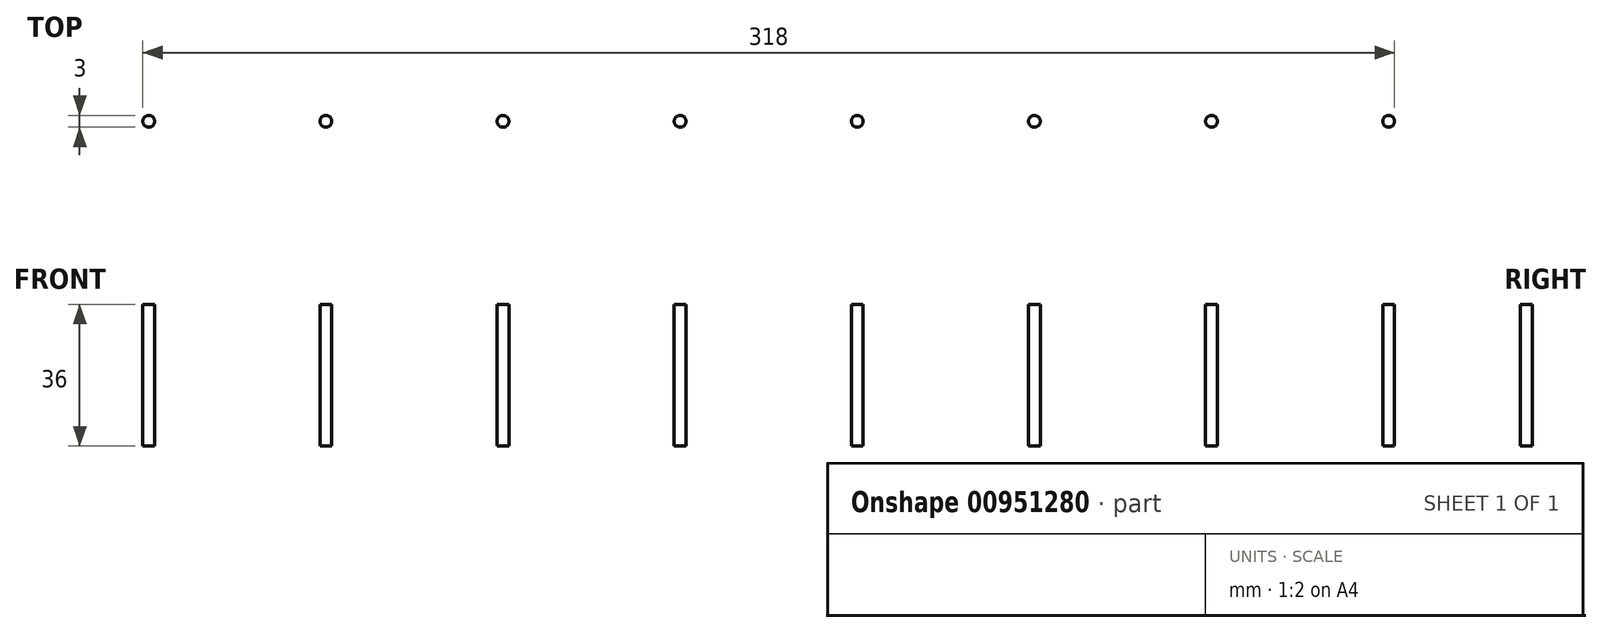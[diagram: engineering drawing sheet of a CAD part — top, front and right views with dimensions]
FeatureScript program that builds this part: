
annotation { "Feature Type Name" : "Feature", "Feature Type Description" : "" }
export const myFeature = defineFeature(function(context is Context, id is Id, definition is map)
    precondition{}
    {
        {
            var Q0;
            Q0=qCreatedBy(makeId("Right.planeOp"),FACE);
            var sketch = newSketch(context, id + "F0", { "sketchPlane" : qUnion([Q0])});
            skLineSegment(sketch, "E0.bottom", {"start": v(36.5, -18) * mm, "end": v(-36.5, -18) * mm});
            skLineSegment(sketch, "E0.top", {"start": v(36.5, 18) * mm, "end": v(-36.5, 18) * mm});
            skLineSegment(sketch, "E0.left", {"start": v(36.5, -18) * mm, "end": v(36.5, 18) * mm});
            skLineSegment(sketch, "E0.right", {"start": v(-36.5, -18) * mm, "end": v(-36.5, 18) * mm});
            skPoint(sketch, "E0.middle", {"position": v(0, 0) * mm});
            skSolve(sketch);
        }
        {
            var Q0;
            Q0=makeQuery(id+"F0.imprint","IMPRINT",FACE,{"disambiguationData":[TD([[makeQuery(id+"F0.imprint","IMPRINT",EDGE,{"derivedFrom":sQuery(id+"F0.wireOp",EDGE,"E0.bottom")}),-1.0]])]});
            extrude(context, id + "F1", {"entities" : qUnion([Q0]), "depth" : 660 * mm, "offsetDistance" : 25 * mm});
        }
        {
            var Q0;
            Q0=makeQuery(id+"F1.opExtrude","SWEPT_FACE",FACE,{"disambiguationData":[OSD([sQuery(id+"F0.wireOp",EDGE,"E0.top")])]});
            var sketch = newSketch(context, id + "F2", { "sketchPlane" : qUnion([Q0])});
            skLineSegment(sketch, "E1", {"start": v(0, -36.5) * mm, "end": v(0, 3.5) * mm, "construction": true});
            skLineSegment(sketch, "E2", {"start": v(0, 3.5) * mm, "end": v(40, 3.5) * mm, "construction": true});
            skCircle(sketch, "E3", {"center": v(40, 3.5) * mm, "radius": 2.5 * mm});
            skLineSegment(sketch, "E4", {"start": v(330, -36.5) * mm, "end": v(330, 36.5) * mm});
            skPoint(sketch, "E5.endSnap0", {"position": v(660, 0) * mm});
            skLineSegment(sketch, "E6", {"start": v(660, 3.5) * mm, "end": v(620, 3.5) * mm, "construction": true});
            skCircle(sketch, "E7", {"center": v(620, 3.5) * mm, "radius": 2.5 * mm});
            skLineSegment(sketch, "E8", {"start": v(0, 9.17) * mm, "end": v(15, 9.17) * mm, "construction": true});
            skLineSegment(sketch, "E9", {"start": v(15, 9.17) * mm, "end": v(30, 9.17) * mm, "construction": true});
            skLineSegment(sketch, "E10", {"start": v(30, 9.17) * mm, "end": v(45, 9.17) * mm, "construction": true});
            skLineSegment(sketch, "E11", {"start": v(45, 9.17) * mm, "end": v(60, 9.17) * mm, "construction": true});
            skLineSegment(sketch, "E12", {"start": v(60, 9.17) * mm, "end": v(75, 9.17) * mm, "construction": true});
            skLineSegment(sketch, "E13", {"start": v(75, 9.17) * mm, "end": v(90, 9.17) * mm, "construction": true});
            skLineSegment(sketch, "E14", {"start": v(90, 9.17) * mm, "end": v(105, 9.17) * mm, "construction": true});
            skLineSegment(sketch, "E15", {"start": v(105, 9.17) * mm, "end": v(120, 9.17) * mm, "construction": true});
            skLineSegment(sketch, "E16", {"start": v(120, 9.17) * mm, "end": v(135, 9.17) * mm, "construction": true});
            skLineSegment(sketch, "E17", {"start": v(135, 9.17) * mm, "end": v(150, 9.17) * mm, "construction": true});
            skLineSegment(sketch, "E18", {"start": v(150, 9.17) * mm, "end": v(165, 9.17) * mm, "construction": true});
            skLineSegment(sketch, "E19", {"start": v(165, 9.17) * mm, "end": v(180, 9.17) * mm, "construction": true});
            skLineSegment(sketch, "E20", {"start": v(180, 9.17) * mm, "end": v(195, 9.17) * mm, "construction": true});
            skLineSegment(sketch, "E21", {"start": v(195, 9.17) * mm, "end": v(210, 9.17) * mm, "construction": true});
            skLineSegment(sketch, "E22", {"start": v(210, 9.17) * mm, "end": v(225, 9.17) * mm, "construction": true});
            skLineSegment(sketch, "E23", {"start": v(225, 9.17) * mm, "end": v(240, 9.17) * mm, "construction": true});
            skLineSegment(sketch, "E24", {"start": v(240, 9.17) * mm, "end": v(255, 9.17) * mm, "construction": true});
            skLineSegment(sketch, "E25", {"start": v(255, 9.17) * mm, "end": v(270, 9.17) * mm, "construction": true});
            skLineSegment(sketch, "E26", {"start": v(270, 9.17) * mm, "end": v(285, 9.17) * mm, "construction": true});
            skLineSegment(sketch, "E27", {"start": v(285, 9.17) * mm, "end": v(300, 9.17) * mm, "construction": true});
            skLineSegment(sketch, "E28", {"start": v(300, 9.17) * mm, "end": v(315, 9.17) * mm, "construction": true});
            skLineSegment(sketch, "E29", {"start": v(315, 9.17) * mm, "end": v(330, 9.17) * mm, "construction": true});
            skCircle(sketch, "E30", {"center": v(15, 3.5) * mm, "radius": 1.5 * mm});
            skLineSegment(sketch, "E31", {"start": v(40, 3.5) * mm, "end": v(330, 3.5) * mm, "construction": true});
            skCircle(sketch, "E32", {"center": v(60, 3.5) * mm, "radius": 1.5 * mm});
            skCircle(sketch, "E33", {"center": v(105, 3.5) * mm, "radius": 1.5 * mm});
            skCircle(sketch, "E34", {"center": v(150, 3.5) * mm, "radius": 1.5 * mm});
            skCircle(sketch, "E35", {"center": v(195, 3.5) * mm, "radius": 1.5 * mm});
            skCircle(sketch, "E36", {"center": v(240, 3.5) * mm, "radius": 1.5 * mm});
            skCircle(sketch, "E37", {"center": v(285, 3.5) * mm, "radius": 1.5 * mm});
            skCircle(sketch, "E38", {"center": v(330, 3.5) * mm, "radius": 1.5 * mm});
            skCircle(sketch, "E39.MirrorC", {"center": v(375, 3.5) * mm, "radius": 1.5 * mm});
            skCircle(sketch, "E40.MirrorC", {"center": v(420, 3.5) * mm, "radius": 1.5 * mm});
            skCircle(sketch, "E41.MirrorC", {"center": v(465, 3.5) * mm, "radius": 1.5 * mm});
            skCircle(sketch, "E42.MirrorC", {"center": v(510, 3.5) * mm, "radius": 1.5 * mm});
            skCircle(sketch, "E43.MirrorC", {"center": v(555, 3.5) * mm, "radius": 1.5 * mm});
            skCircle(sketch, "E44.MirrorC", {"center": v(600, 3.5) * mm, "radius": 1.5 * mm});
            skCircle(sketch, "E45.MirrorC", {"center": v(645, 3.5) * mm, "radius": 1.5 * mm});
            skSolve(sketch);
        }
        {
            var Q0;
            Q0=makeQuery(id+"F2.imprint","IMPRINT",FACE,{"disambiguationData":[TD([[makeQuery(id+"F2.imprint","IMPRINT",EDGE,{"derivedFrom":sQuery(id+"F2.wireOp",EDGE,"E30")}),1.0]])]});
            var Q1;
            Q1=makeQuery(id+"F2.imprint","IMPRINT",FACE,{"disambiguationData":[TD([[makeQuery(id+"F2.imprint","IMPRINT",EDGE,{"derivedFrom":sQuery(id+"F2.wireOp",EDGE,"E3")}),1.0]])]});
            var Q2;
            Q2=makeQuery(id+"F2.imprint","IMPRINT",FACE,{"disambiguationData":[TD([[makeQuery(id+"F2.imprint","IMPRINT",EDGE,{"derivedFrom":sQuery(id+"F2.wireOp",EDGE,"E32")}),1.0]])]});
            var Q3;
            Q3=makeQuery(id+"F2.imprint","IMPRINT",FACE,{"disambiguationData":[TD([[makeQuery(id+"F2.imprint","IMPRINT",EDGE,{"derivedFrom":sQuery(id+"F2.wireOp",EDGE,"E34")}),1.0]])]});
            var Q4;
            Q4=makeQuery(id+"F2.imprint","IMPRINT",FACE,{"disambiguationData":[TD([[makeQuery(id+"F2.imprint","IMPRINT",EDGE,{"derivedFrom":sQuery(id+"F2.wireOp",EDGE,"E33")}),1.0]])]});
            var Q5;
            Q5=makeQuery(id+"F2.imprint","IMPRINT",FACE,{"disambiguationData":[TD([[makeQuery(id+"F2.imprint","IMPRINT",EDGE,{"derivedFrom":sQuery(id+"F2.wireOp",EDGE,"E35")}),1.0]])]});
            var Q6;
            Q6=makeQuery(id+"F2.imprint","IMPRINT",FACE,{"disambiguationData":[TD([[makeQuery(id+"F2.imprint","IMPRINT",EDGE,{"derivedFrom":sQuery(id+"F2.wireOp",EDGE,"E36")}),1.0]])]});
            var Q7;
            Q7=makeQuery(id+"F2.imprint","IMPRINT",FACE,{"disambiguationData":[TD([[makeQuery(id+"F2.imprint","IMPRINT",EDGE,{"derivedFrom":sQuery(id+"F2.wireOp",EDGE,"E37")}),1.0]])]});
            var Q8;
            {var subQ0=sQuery(id+"F2.wireOp",EDGE,"E38");var subQ1=sQuery(id+"F2.wireOp",EDGE,"E4");var subQ2=makeQuery(id+"F2.imprint","INTERSECT",VERTEX,{"disambiguationData":[OD(0.0)],"derivedFrom":[subQ1,subQ0]});Q8=makeQuery(id+"F2.imprint","IMPRINT",FACE,{"disambiguationData":[TD([[makeQuery(id+"F2.imprint","IMPRINT",EDGE,{"disambiguationData":[TD([[subQ2,-1.0]])],"derivedFrom":subQ1}),1.0]])]});}
            var Q9;
            Q9=makeQuery(id+"F2.imprint","IMPRINT",FACE,{"disambiguationData":[TD([[makeQuery(id+"F2.imprint","IMPRINT",EDGE,{"derivedFrom":sQuery(id+"F2.wireOp",EDGE,"E39.MirrorC")}),-1.0]])]});
            var Q10;
            {var subQ0=sQuery(id+"F2.wireOp",EDGE,"E38");var subQ1=sQuery(id+"F2.wireOp",EDGE,"E4");var subQ2=makeQuery(id+"F2.imprint","INTERSECT",VERTEX,{"disambiguationData":[OD(0.0)],"derivedFrom":[subQ1,subQ0]});Q10=makeQuery(id+"F2.imprint","IMPRINT",FACE,{"disambiguationData":[TD([[makeQuery(id+"F2.imprint","IMPRINT",EDGE,{"disambiguationData":[TD([[subQ2,-1.0]])],"derivedFrom":subQ1}),-1.0]])]});}
            var Q11;
            Q11=makeQuery(id+"F2.imprint","IMPRINT",FACE,{"disambiguationData":[TD([[makeQuery(id+"F2.imprint","IMPRINT",EDGE,{"derivedFrom":sQuery(id+"F2.wireOp",EDGE,"E40.MirrorC")}),-1.0]])]});
            var Q12;
            Q12=makeQuery(id+"F2.imprint","IMPRINT",FACE,{"disambiguationData":[TD([[makeQuery(id+"F2.imprint","IMPRINT",EDGE,{"derivedFrom":sQuery(id+"F2.wireOp",EDGE,"E41.MirrorC")}),-1.0]])]});
            var Q13;
            Q13=makeQuery(id+"F2.imprint","IMPRINT",FACE,{"disambiguationData":[TD([[makeQuery(id+"F2.imprint","IMPRINT",EDGE,{"derivedFrom":sQuery(id+"F2.wireOp",EDGE,"E42.MirrorC")}),-1.0]])]});
            var Q14;
            Q14=makeQuery(id+"F2.imprint","IMPRINT",FACE,{"disambiguationData":[TD([[makeQuery(id+"F2.imprint","IMPRINT",EDGE,{"derivedFrom":sQuery(id+"F2.wireOp",EDGE,"E43.MirrorC")}),-1.0]])]});
            var Q15;
            Q15=makeQuery(id+"F2.imprint","IMPRINT",FACE,{"disambiguationData":[TD([[makeQuery(id+"F2.imprint","IMPRINT",EDGE,{"derivedFrom":sQuery(id+"F2.wireOp",EDGE,"E44.MirrorC")}),-1.0]])]});
            var Q16;
            Q16=makeQuery(id+"F2.imprint","IMPRINT",FACE,{"disambiguationData":[TD([[makeQuery(id+"F2.imprint","IMPRINT",EDGE,{"derivedFrom":sQuery(id+"F2.wireOp",EDGE,"E7")}),1.0]])]});
            var Q17;
            Q17=makeQuery(id+"F2.imprint","IMPRINT",FACE,{"disambiguationData":[TD([[makeQuery(id+"F2.imprint","IMPRINT",EDGE,{"derivedFrom":sQuery(id+"F2.wireOp",EDGE,"E45.MirrorC")}),-1.0]])]});
            extrude(context, id + "F3", {"entities" : qUnion([Q0, Q1, Q2, Q3, Q4, Q5, Q6, Q7, Q8, Q9, Q10, Q11, Q12, Q13, Q14, Q15, Q16, Q17]), "operationType" : NewBodyOperationType.REMOVE, "oppositeDirection" : true, "depth" : 40 * mm, "offsetDistance" : 25 * mm});
        }
    });
